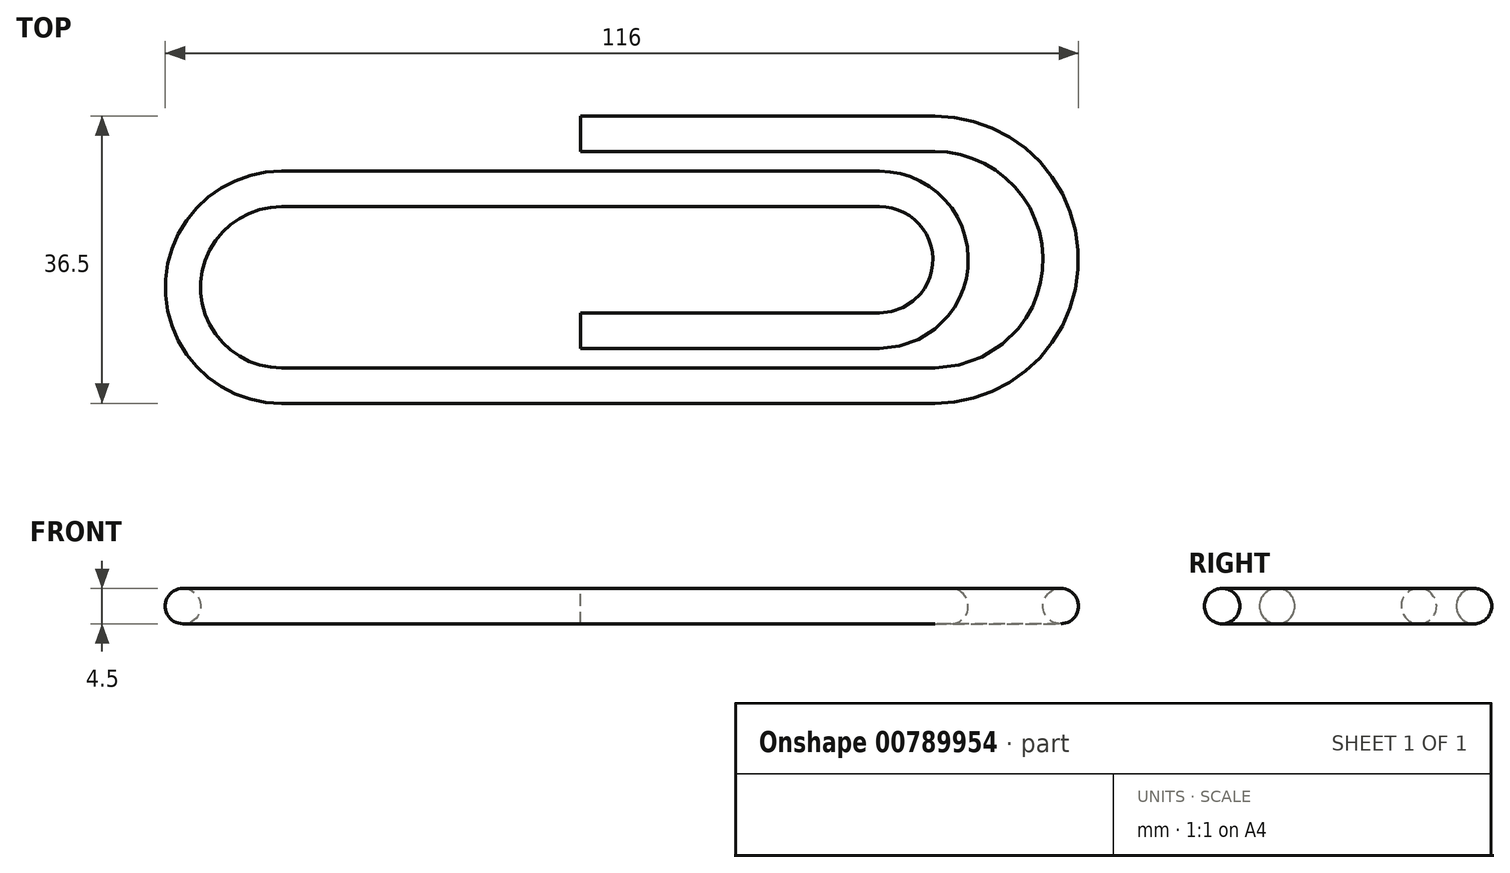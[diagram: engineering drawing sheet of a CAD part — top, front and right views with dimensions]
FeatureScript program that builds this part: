
annotation { "Feature Type Name" : "Feature", "Feature Type Description" : "" }
export const myFeature = defineFeature(function(context is Context, id is Id, definition is map)
    precondition{}
    {
        {
            var Q0;
            Q0=qCreatedBy(makeId("Right.planeOp"),FACE);
            var sketch = newSketch(context, id + "F0", { "sketchPlane" : qUnion([Q0])});
            skCircle(sketch, "E0", {"center": v(0, 0) * mm, "radius": 2.25 * mm});
            skSolve(sketch);
        }
        {
            var Q0;
            Q0=qCreatedBy(makeId("Top.planeOp"),FACE);
            var sketch = newSketch(context, id + "F1", { "sketchPlane" : qUnion([Q0])});
            skLineSegment(sketch, "E1", {"start": v(0, 0) * mm, "end": v(38, 0) * mm});
            skLineSegment(sketch, "E2", {"start": v(38, 18) * mm, "end": v(-38, 18) * mm});
            skLineSegment(sketch, "E3", {"start": v(-38, -7) * mm, "end": v(45, -7) * mm});
            skLineSegment(sketch, "E4", {"start": v(45, 25) * mm, "end": v(0, 25) * mm});
            skArc(sketch, "E5", {"start": v(-38, 18) * mm, "mid": v(-50.5, 5.5) * mm, "end": v(-38, -7) * mm});
            skArc(sketch, "E6", {"start": v(45, -7) * mm, "mid": v(61, 9) * mm, "end": v(45, 25) * mm});
            skArc(sketch, "E7", {"start": v(38, 0) * mm, "mid": v(47, 9) * mm, "end": v(38, 18) * mm});
            skSolve(sketch);
        }
        {
            var Q0;
            Q0 = qSketchRegion(id + "F0", true);
            var Q1;
            Q1 = qConstructionFilter(qBodyType(qCreatedBy(id + "F1" ,EDGE), BodyType.WIRE), ConstructionObject.NO);
            sweep(context, id + "F2", {"profiles" : qUnion([Q0]), "path" : qUnion([Q1])});
        }
    });
